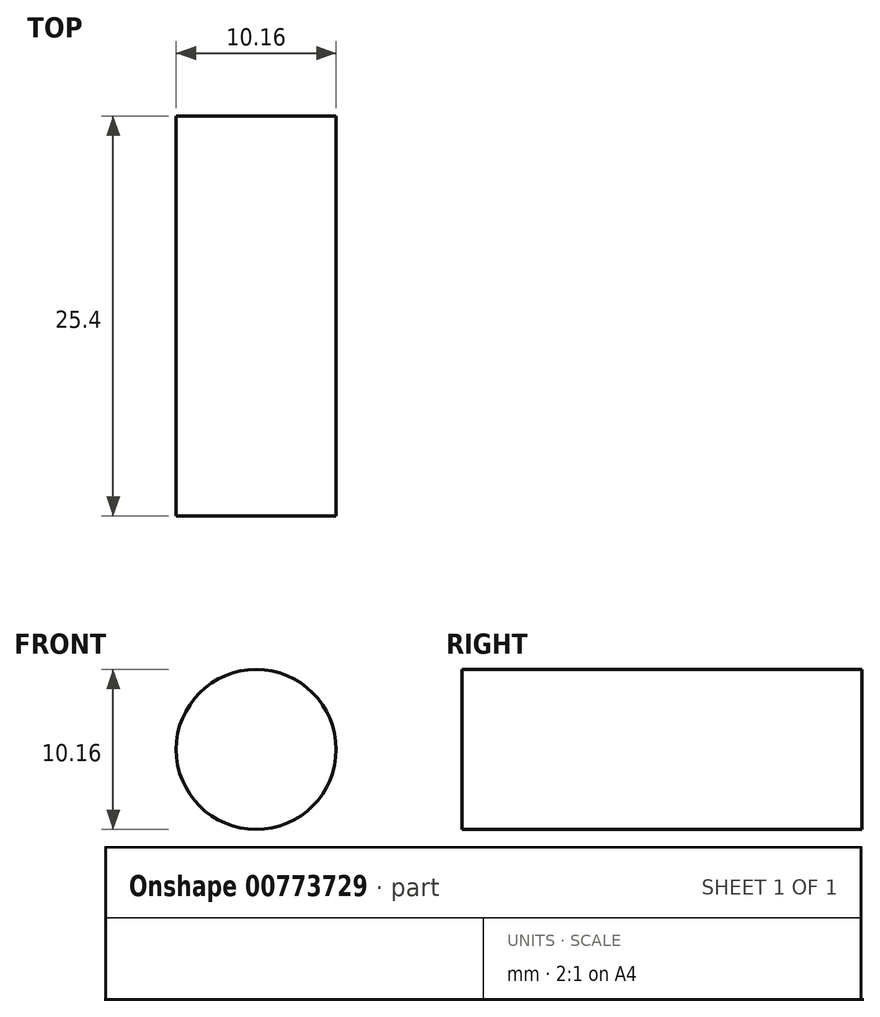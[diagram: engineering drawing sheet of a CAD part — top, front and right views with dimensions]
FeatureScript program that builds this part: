
annotation { "Feature Type Name" : "Feature", "Feature Type Description" : "" }
export const myFeature = defineFeature(function(context is Context, id is Id, definition is map)
    precondition{}
    {
        {
            var Q0;
            Q0=qCreatedBy(makeId("Front.planeOp"),FACE);
            var sketch = newSketch(context, id + "F0", { "sketchPlane" : qUnion([Q0])});
            skCircle(sketch, "E0", {"center": v(0, 0) * mm, "radius": 5.08 * mm});
            skSolve(sketch);
        }
        {
            var Q0;
            Q0=makeQuery(id+"F0.imprint","IMPRINT",FACE,{"disambiguationData":[TD([[makeQuery(id+"F0.imprint","IMPRINT",EDGE,{"derivedFrom":sQuery(id+"F0.wireOp",EDGE,"E0")}),1.0]])]});
            extrude(context, id + "F1", {"entities" : qUnion([Q0]), "depth" : 25.4 * mm, "offsetDistance" : 25.4 * mm});
        }
    });
